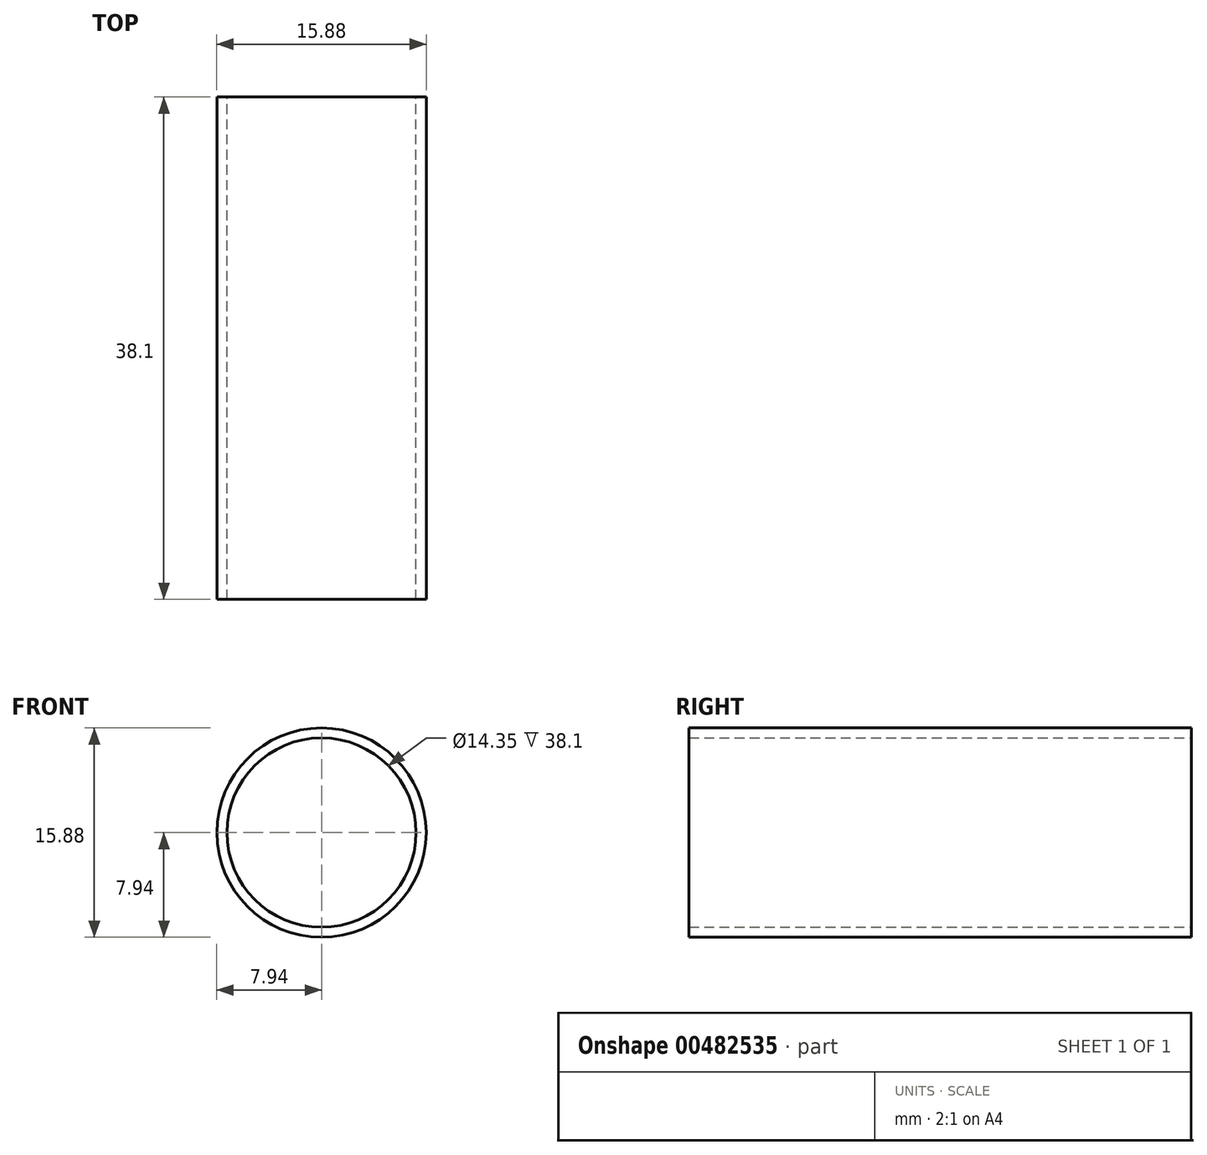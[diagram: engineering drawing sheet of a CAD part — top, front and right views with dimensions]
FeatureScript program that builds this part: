
annotation { "Feature Type Name" : "Feature", "Feature Type Description" : "" }
export const myFeature = defineFeature(function(context is Context, id is Id, definition is map)
    precondition{}
    {
        {
            var Q0;
            Q0=qCreatedBy(makeId("Front.planeOp"),FACE);
            var sketch = newSketch(context, id + "F0", { "sketchPlane" : qUnion([Q0])});
            skCircle(sketch, "E0", {"center": v(0, 0) * mm, "radius": 7.94 * mm});
            skCircle(sketch, "E1.0", {"center": v(0, 0) * mm, "radius": 7.18 * mm});
            skSolve(sketch);
        }
        {
            var Q0;
            Q0=makeQuery(id+"F0.imprint","IMPRINT",FACE,{"disambiguationData":[TD([[makeQuery(id+"F0.imprint","IMPRINT",EDGE,{"derivedFrom":sQuery(id+"F0.wireOp",EDGE,"E0")}),1.0]])]});
            extrude(context, id + "F1", {"entities" : qUnion([Q0]), "depth" : 38.1 * mm});
        }
    });
